# Revit family: Auto-Door_Sliding_BiPart_CurtainWall_Tormax_TX9200
name_source: partatom
category: Doors
units: mm (PartAtom-declared; Revit-internal decimal feet)

## family parameters
Always vertical = Yes
Classification Number = 23.30.10.17.11
Cut with Voids When Loaded = No
Room Calculation Point = No
Shared = No

## types (1)
- Type as Specified
    Access Control = No
    Air Infiltration = as Specified
    Analytic Construction = <None>
    Assembly Code = B2030110
    Available Options = as Specified
    Construction Details = http://www.arcat.com
    Define Thermal Properties by = Schematic Type
    Description = Tormax Automatic Sliding Door as Specified in 08463
    Expected Lifespan (Years) = 0
    Frame Thickness = 0' - 4 1/2"
    Function = Interior
    Green Building-LEED = http://www.arcat.com
    HD Drive = No
    Has Partial Breakout Capability = Yes
    Include Transom = Yes
    Keynote = 08463
    Maintenance Schedule (Months) = 0
    Manufacturer = TORMAX USA Inc.
    Manufacturer Fax = 210-494-5930
    Manufacturer Website = http://www.tormaxusa.com
    Miami Dade Conformance = as Specified
    Model = As Specified in 08463
    Operating Temperature Range = as Specified
    Panel Thickness = 0' - 1 3/4"
    Product Data = http://www.arcat.com
    RO Spacing_Sides = 0' - 0 1/4"
    RO Spacing_Top = 0' - 0 1/4"
    Revision = R1_02-2014
    Sales Information = http://www.tormaxusa.com
    Send Message = http://www.arcat.com
    Specification = http://www.arcat.com
    Standards Conformance = as Specified
    Storm Door = No
    Storm Impact Door = No
    Structural Test Pressure = as Specified
    Thickness = 0' - 4 1/2"
    URL = http://www.tormaxusa.com
    Warranty Duration (Years) = 0
    Water Penetration = as Specified
    headerdepth = 0' - 8"

## geometry (parser evidence)
native form markers: Blend x2, Sweep x5
no freeform markers — native parametric forms only
